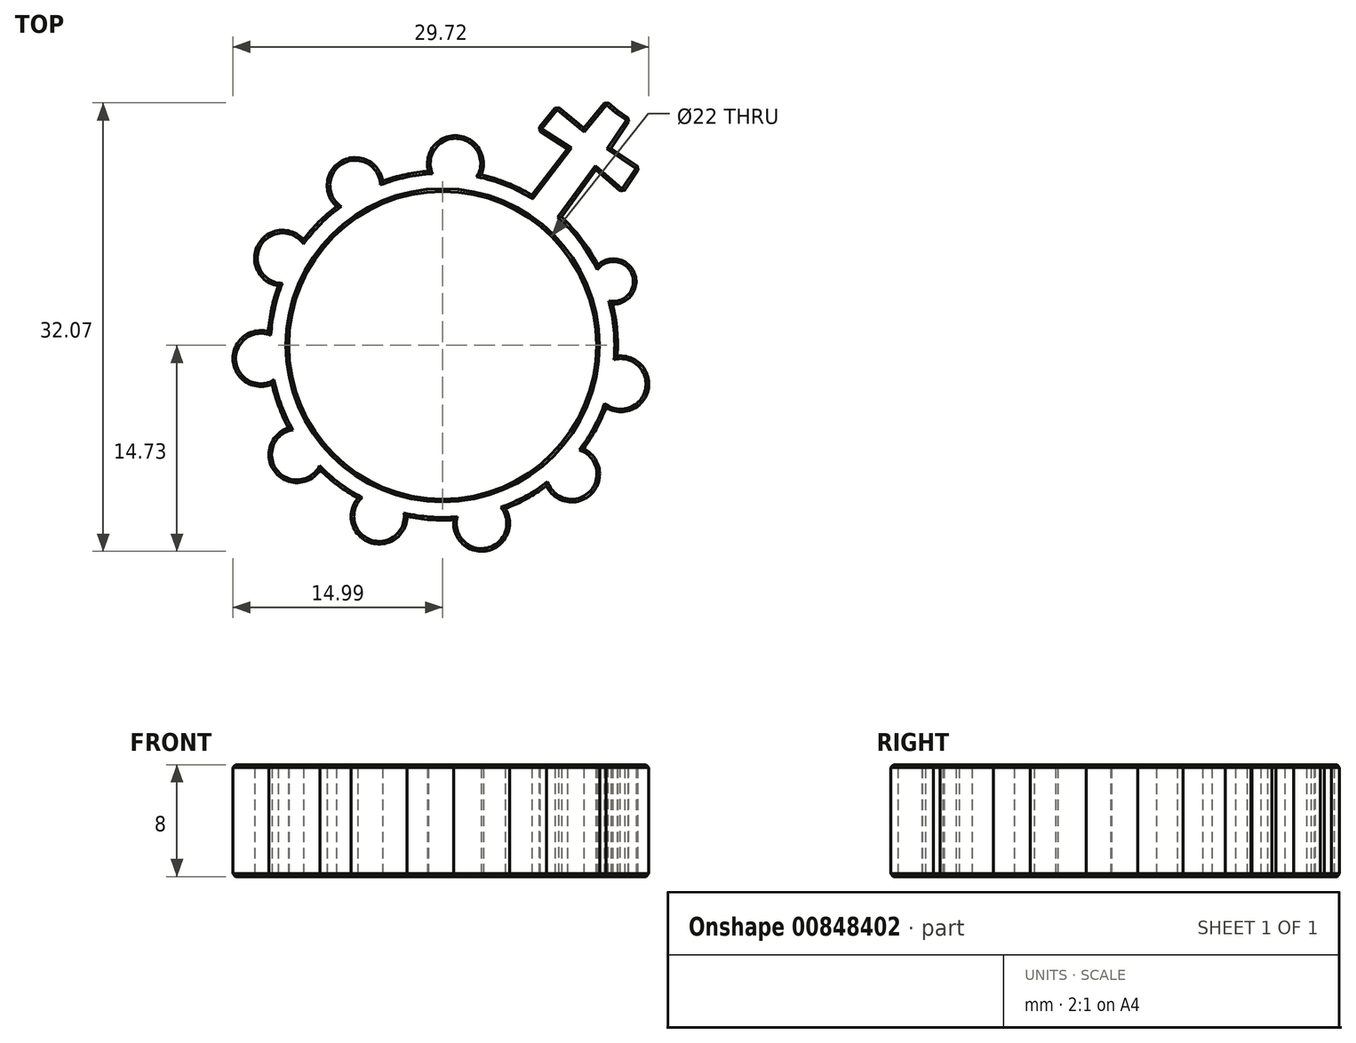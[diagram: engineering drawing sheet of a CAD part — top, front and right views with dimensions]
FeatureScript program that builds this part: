
annotation { "Feature Type Name" : "Feature", "Feature Type Description" : "" }
export const myFeature = defineFeature(function(context is Context, id is Id, definition is map)
    precondition{}
    {
        {
            var Q0;
            Q0=qCreatedBy(makeId("Top.planeOp"),FACE);
            var sketch = newSketch(context, id + "F0", { "sketchPlane" : qUnion([Q0])});
            skCircle(sketch, "E0", {"center": v(0, 0) * mm, "radius": 11 * mm});
            skCircle(sketch, "E1", {"center": v(0, 0) * mm, "radius": 12.5 * mm});
            skCircle(sketch, "E2.cCircle", {"center": v(0, 0) * mm, "radius": 12.5 * mm, "construction": true});
            skLineSegment(sketch, "E2.0", {"start": v(9.22, -9.2) * mm, "end": v(2.78, -12.73) * mm});
            skLineSegment(sketch, "E2.1", {"start": v(2.78, -12.73) * mm, "end": v(-4.54, -12.21) * mm});
            skLineSegment(sketch, "E2.2", {"start": v(-4.54, -12.21) * mm, "end": v(-10.42, -7.82) * mm});
            skLineSegment(sketch, "E2.3", {"start": v(-10.42, -7.82) * mm, "end": v(-13, -0.94) * mm});
            skLineSegment(sketch, "E2.4", {"start": v(-13, -0.94) * mm, "end": v(-11.44, 6.23) * mm});
            skLineSegment(sketch, "E2.5", {"start": v(-11.44, 6.23) * mm, "end": v(-6.25, 11.43) * mm});
            skLineSegment(sketch, "E2.6", {"start": v(-6.25, 11.43) * mm, "end": v(0.92, 13) * mm});
            skLineSegment(sketch, "E2.7", {"start": v(0.92, 13) * mm, "end": v(7.8, 10.44) * mm});
            skLineSegment(sketch, "E2.8", {"start": v(7.8, 10.44) * mm, "end": v(12.2, 4.56) * mm});
            skLineSegment(sketch, "E2.9", {"start": v(12.2, 4.56) * mm, "end": v(12.73, -2.76) * mm});
            skLineSegment(sketch, "E2.10", {"start": v(12.73, -2.76) * mm, "end": v(9.22, -9.2) * mm});
            skPoint(sketch, "E2.0.midPoint", {"position": v(6, -10.97) * mm});
            skCircle(sketch, "E3", {"center": v(0.92, 13) * mm, "radius": 2 * mm});
            skCircle(sketch, "E4", {"center": v(-6.25, 11.43) * mm, "radius": 2 * mm});
            skCircle(sketch, "E5", {"center": v(-11.44, 6.23) * mm, "radius": 2 * mm});
            skCircle(sketch, "E6", {"center": v(-13, -0.94) * mm, "radius": 2 * mm});
            skCircle(sketch, "E7", {"center": v(-10.42, -7.82) * mm, "radius": 2 * mm});
            skCircle(sketch, "E8", {"center": v(-4.54, -12.21) * mm, "radius": 2 * mm});
            skCircle(sketch, "E9", {"center": v(2.78, -12.73) * mm, "radius": 2 * mm});
            skCircle(sketch, "E10", {"center": v(9.22, -9.2) * mm, "radius": 2 * mm});
            skCircle(sketch, "E11", {"center": v(12.73, -2.76) * mm, "radius": 2 * mm});
            skCircle(sketch, "E12", {"center": v(12.2, 4.56) * mm, "radius": 1.62 * mm});
            skLineSegment(sketch, "E13", {"start": v(0, 0) * mm, "end": v(12.63, 16.93) * mm, "construction": true});
            skLineSegment(sketch, "E14", {"start": v(6.38, 10.75) * mm, "end": v(8.92, 14.06) * mm});
            skLineSegment(sketch, "E15", {"start": v(8.92, 14.06) * mm, "end": v(6.77, 15.44) * mm});
            skLineSegment(sketch, "E16", {"start": v(6.77, 15.44) * mm, "end": v(8.16, 17.12) * mm});
            skLineSegment(sketch, "E17", {"start": v(8.16, 17.12) * mm, "end": v(10.08, 15.53) * mm});
            skLineSegment(sketch, "E18", {"start": v(10.08, 15.53) * mm, "end": v(11.67, 17.46) * mm});
            skLineSegment(sketch, "E19", {"start": v(11.67, 17.46) * mm, "end": v(12.51, 16.77) * mm});
            skLineSegment(sketch, "E20.MirrorCS", {"start": v(13.41, 16.16) * mm, "end": v(12.51, 16.77) * mm});
            skLineSegment(sketch, "E21.MirrorCS", {"start": v(12.02, 14.1) * mm, "end": v(13.41, 16.16) * mm});
            skLineSegment(sketch, "E22.MirrorCS", {"start": v(14.09, 12.7) * mm, "end": v(12.02, 14.1) * mm});
            skLineSegment(sketch, "E23.MirrorCS", {"start": v(12.87, 10.9) * mm, "end": v(14.09, 12.7) * mm});
            skLineSegment(sketch, "E24.MirrorCS", {"start": v(10.94, 12.56) * mm, "end": v(12.87, 10.9) * mm});
            skLineSegment(sketch, "E25.MirrorCS", {"start": v(8.49, 9.18) * mm, "end": v(10.94, 12.56) * mm});
            skSolve(sketch);
        }
        {
            var Q0;
            Q0=makeQuery(id+"F0.imprint","IMPRINT",FACE,{"disambiguationData":[TD([[makeQuery(id+"F0.imprint","IMPRINT",EDGE,{"derivedFrom":sQuery(id+"F0.wireOp",EDGE,"E0")}),-1.0]])]});
            var Q1;
            {var subQ0=sQuery(id+"F0.wireOp",EDGE,"E2.7");var subQ1=sQuery(id+"F0.wireOp",EDGE,"E2.6");var subQ2=makeQuery(id+"F0.imprint","INTERSECT",VERTEX,{"derivedFrom":[subQ1,subQ0]});Q1=makeQuery(id+"F0.imprint","IMPRINT",FACE,{"disambiguationData":[TD([[makeQuery(id+"F0.imprint","IMPRINT",EDGE,{"disambiguationData":[TD([[subQ2,1.0]])],"derivedFrom":subQ1}),1.0]])]});}
            var Q2;
            {var subQ5=sQuery(id+"F0.wireOp",EDGE,"E15");Q2=makeQuery(id+"F0.imprint","IMPRINT",FACE,{"disambiguationData":[TD([[makeQuery(id+"F0.imprint","IMPRINT",EDGE,{"derivedFrom":subQ5}),-1.0]])]});}
            var Q3;
            {var subQ0=sQuery(id+"F0.wireOp",EDGE,"E14");var subQ1=sQuery(id+"F0.wireOp",EDGE,"E1");var subQ2=makeQuery(id+"F0.imprint","INTERSECT",VERTEX,{"derivedFrom":[subQ1,subQ0]});Q3=makeQuery(id+"F0.imprint","IMPRINT",FACE,{"disambiguationData":[TD([[makeQuery(id+"F0.imprint","IMPRINT",EDGE,{"disambiguationData":[TD([[subQ2,1.0]])],"derivedFrom":subQ1}),-1.0]])]});}
            var Q4;
            {var subQ0=sQuery(id+"F0.wireOp",EDGE,"E2.9");var subQ1=sQuery(id+"F0.wireOp",EDGE,"E2.8");var subQ2=makeQuery(id+"F0.imprint","INTERSECT",VERTEX,{"derivedFrom":[subQ1,subQ0]});Q4=makeQuery(id+"F0.imprint","IMPRINT",FACE,{"disambiguationData":[TD([[makeQuery(id+"F0.imprint","IMPRINT",EDGE,{"disambiguationData":[TD([[subQ2,1.0]])],"derivedFrom":subQ1}),1.0]])]});}
            var Q5;
            {var subQ0=sQuery(id+"F0.wireOp",EDGE,"E12");var subQ1=sQuery(id+"F0.wireOp",EDGE,"E1");var subQ2=makeQuery(id+"F0.imprint","INTERSECT",VERTEX,{"disambiguationData":[OD(0.0)],"derivedFrom":[subQ1,subQ0]});Q5=makeQuery(id+"F0.imprint","IMPRINT",FACE,{"disambiguationData":[TD([[makeQuery(id+"F0.imprint","IMPRINT",EDGE,{"disambiguationData":[TD([[subQ2,-1.0]])],"derivedFrom":subQ1}),1.0]])]});}
            var Q6;
            {var subQ0=sQuery(id+"F0.wireOp",EDGE,"E2.10");var subQ1=sQuery(id+"F0.wireOp",EDGE,"E2.9");var subQ2=makeQuery(id+"F0.imprint","INTERSECT",VERTEX,{"derivedFrom":[subQ1,subQ0]});Q6=makeQuery(id+"F0.imprint","IMPRINT",FACE,{"disambiguationData":[TD([[makeQuery(id+"F0.imprint","IMPRINT",EDGE,{"disambiguationData":[TD([[subQ2,1.0]])],"derivedFrom":subQ1}),1.0]])]});}
            var Q7;
            {var subQ0=sQuery(id+"F0.wireOp",EDGE,"E2.10");var subQ1=sQuery(id+"F0.wireOp",EDGE,"E2.0");var subQ2=makeQuery(id+"F0.imprint","INTERSECT",VERTEX,{"derivedFrom":[subQ1,subQ0]});Q7=makeQuery(id+"F0.imprint","IMPRINT",FACE,{"disambiguationData":[TD([[makeQuery(id+"F0.imprint","IMPRINT",EDGE,{"disambiguationData":[TD([[subQ2,-1.0]])],"derivedFrom":subQ1}),1.0]])]});}
            var Q8;
            {var subQ0=sQuery(id+"F0.wireOp",EDGE,"E2.1");var subQ1=sQuery(id+"F0.wireOp",EDGE,"E2.0");var subQ2=makeQuery(id+"F0.imprint","INTERSECT",VERTEX,{"derivedFrom":[subQ1,subQ0]});Q8=makeQuery(id+"F0.imprint","IMPRINT",FACE,{"disambiguationData":[TD([[makeQuery(id+"F0.imprint","IMPRINT",EDGE,{"disambiguationData":[TD([[subQ2,1.0]])],"derivedFrom":subQ1}),1.0]])]});}
            var Q9;
            {var subQ0=sQuery(id+"F0.wireOp",EDGE,"E2.2");var subQ1=sQuery(id+"F0.wireOp",EDGE,"E2.1");var subQ2=makeQuery(id+"F0.imprint","INTERSECT",VERTEX,{"derivedFrom":[subQ1,subQ0]});Q9=makeQuery(id+"F0.imprint","IMPRINT",FACE,{"disambiguationData":[TD([[makeQuery(id+"F0.imprint","IMPRINT",EDGE,{"disambiguationData":[TD([[subQ2,1.0]])],"derivedFrom":subQ1}),1.0]])]});}
            var Q10;
            {var subQ0=sQuery(id+"F0.wireOp",EDGE,"E2.3");var subQ1=sQuery(id+"F0.wireOp",EDGE,"E2.2");var subQ2=makeQuery(id+"F0.imprint","INTERSECT",VERTEX,{"derivedFrom":[subQ1,subQ0]});Q10=makeQuery(id+"F0.imprint","IMPRINT",FACE,{"disambiguationData":[TD([[makeQuery(id+"F0.imprint","IMPRINT",EDGE,{"disambiguationData":[TD([[subQ2,1.0]])],"derivedFrom":subQ1}),1.0]])]});}
            var Q11;
            {var subQ0=sQuery(id+"F0.wireOp",EDGE,"E2.4");var subQ1=sQuery(id+"F0.wireOp",EDGE,"E2.3");var subQ2=makeQuery(id+"F0.imprint","INTERSECT",VERTEX,{"derivedFrom":[subQ1,subQ0]});Q11=makeQuery(id+"F0.imprint","IMPRINT",FACE,{"disambiguationData":[TD([[makeQuery(id+"F0.imprint","IMPRINT",EDGE,{"disambiguationData":[TD([[subQ2,1.0]])],"derivedFrom":subQ1}),1.0]])]});}
            var Q12;
            {var subQ0=sQuery(id+"F0.wireOp",EDGE,"E2.5");var subQ1=sQuery(id+"F0.wireOp",EDGE,"E2.4");var subQ2=makeQuery(id+"F0.imprint","INTERSECT",VERTEX,{"derivedFrom":[subQ1,subQ0]});Q12=makeQuery(id+"F0.imprint","IMPRINT",FACE,{"disambiguationData":[TD([[makeQuery(id+"F0.imprint","IMPRINT",EDGE,{"disambiguationData":[TD([[subQ2,1.0]])],"derivedFrom":subQ1}),1.0]])]});}
            var Q13;
            {var subQ0=sQuery(id+"F0.wireOp",EDGE,"E2.6");var subQ1=sQuery(id+"F0.wireOp",EDGE,"E2.5");var subQ2=makeQuery(id+"F0.imprint","INTERSECT",VERTEX,{"derivedFrom":[subQ1,subQ0]});Q13=makeQuery(id+"F0.imprint","IMPRINT",FACE,{"disambiguationData":[TD([[makeQuery(id+"F0.imprint","IMPRINT",EDGE,{"disambiguationData":[TD([[subQ2,1.0]])],"derivedFrom":subQ1}),1.0]])]});}
            var Q14;
            {var subQ0=sQuery(id+"F0.wireOp",EDGE,"E4");var subQ1=sQuery(id+"F0.wireOp",EDGE,"E1");var subQ2=makeQuery(id+"F0.imprint","INTERSECT",VERTEX,{"disambiguationData":[OD(0.0)],"derivedFrom":[subQ1,subQ0]});Q14=makeQuery(id+"F0.imprint","IMPRINT",FACE,{"disambiguationData":[TD([[makeQuery(id+"F0.imprint","IMPRINT",EDGE,{"disambiguationData":[TD([[subQ2,-1.0]])],"derivedFrom":subQ1}),1.0]])]});}
            var Q15;
            {var subQ0=sQuery(id+"F0.wireOp",EDGE,"E5");var subQ1=sQuery(id+"F0.wireOp",EDGE,"E1");var subQ2=makeQuery(id+"F0.imprint","INTERSECT",VERTEX,{"disambiguationData":[OD(0.0)],"derivedFrom":[subQ1,subQ0]});Q15=makeQuery(id+"F0.imprint","IMPRINT",FACE,{"disambiguationData":[TD([[makeQuery(id+"F0.imprint","IMPRINT",EDGE,{"disambiguationData":[TD([[subQ2,-1.0]])],"derivedFrom":subQ1}),1.0]])]});}
            var Q16;
            {var subQ0=sQuery(id+"F0.wireOp",EDGE,"E6");var subQ1=sQuery(id+"F0.wireOp",EDGE,"E1");var subQ2=makeQuery(id+"F0.imprint","INTERSECT",VERTEX,{"disambiguationData":[OD(0.0)],"derivedFrom":[subQ1,subQ0]});Q16=makeQuery(id+"F0.imprint","IMPRINT",FACE,{"disambiguationData":[TD([[makeQuery(id+"F0.imprint","IMPRINT",EDGE,{"disambiguationData":[TD([[subQ2,-1.0]])],"derivedFrom":subQ1}),1.0]])]});}
            var Q17;
            {var subQ0=sQuery(id+"F0.wireOp",EDGE,"E7");var subQ1=sQuery(id+"F0.wireOp",EDGE,"E1");var subQ2=makeQuery(id+"F0.imprint","INTERSECT",VERTEX,{"disambiguationData":[OD(0.0)],"derivedFrom":[subQ1,subQ0]});Q17=makeQuery(id+"F0.imprint","IMPRINT",FACE,{"disambiguationData":[TD([[makeQuery(id+"F0.imprint","IMPRINT",EDGE,{"disambiguationData":[TD([[subQ2,-1.0]])],"derivedFrom":subQ1}),1.0]])]});}
            var Q18;
            {var subQ0=sQuery(id+"F0.wireOp",EDGE,"E11");var subQ1=sQuery(id+"F0.wireOp",EDGE,"E1");var subQ2=makeQuery(id+"F0.imprint","INTERSECT",VERTEX,{"disambiguationData":[OD(0.0)],"derivedFrom":[subQ1,subQ0]});Q18=makeQuery(id+"F0.imprint","IMPRINT",FACE,{"disambiguationData":[TD([[makeQuery(id+"F0.imprint","IMPRINT",EDGE,{"disambiguationData":[TD([[subQ2,-1.0]])],"derivedFrom":subQ1}),1.0]])]});}
            var Q19;
            {var subQ0=sQuery(id+"F0.wireOp",EDGE,"E8");var subQ1=sQuery(id+"F0.wireOp",EDGE,"E1");var subQ2=makeQuery(id+"F0.imprint","INTERSECT",VERTEX,{"disambiguationData":[OD(0.0)],"derivedFrom":[subQ1,subQ0]});Q19=makeQuery(id+"F0.imprint","IMPRINT",FACE,{"disambiguationData":[TD([[makeQuery(id+"F0.imprint","IMPRINT",EDGE,{"disambiguationData":[TD([[subQ2,-1.0]])],"derivedFrom":subQ1}),1.0]])]});}
            var Q20;
            {var subQ0=sQuery(id+"F0.wireOp",EDGE,"E10");var subQ1=sQuery(id+"F0.wireOp",EDGE,"E1");var subQ2=makeQuery(id+"F0.imprint","INTERSECT",VERTEX,{"disambiguationData":[OD(0.0)],"derivedFrom":[subQ1,subQ0]});Q20=makeQuery(id+"F0.imprint","IMPRINT",FACE,{"disambiguationData":[TD([[makeQuery(id+"F0.imprint","IMPRINT",EDGE,{"disambiguationData":[TD([[subQ2,-1.0]])],"derivedFrom":subQ1}),1.0]])]});}
            var Q21;
            {var subQ0=sQuery(id+"F0.wireOp",EDGE,"E3");var subQ1=sQuery(id+"F0.wireOp",EDGE,"E1");var subQ2=makeQuery(id+"F0.imprint","INTERSECT",VERTEX,{"disambiguationData":[OD(0.0)],"derivedFrom":[subQ1,subQ0]});Q21=makeQuery(id+"F0.imprint","IMPRINT",FACE,{"disambiguationData":[TD([[makeQuery(id+"F0.imprint","IMPRINT",EDGE,{"disambiguationData":[TD([[subQ2,-1.0]])],"derivedFrom":subQ1}),1.0]])]});}
            var Q22;
            {var subQ0=sQuery(id+"F0.wireOp",EDGE,"E9");var subQ1=sQuery(id+"F0.wireOp",EDGE,"E1");var subQ2=makeQuery(id+"F0.imprint","INTERSECT",VERTEX,{"disambiguationData":[OD(0.0)],"derivedFrom":[subQ1,subQ0]});Q22=makeQuery(id+"F0.imprint","IMPRINT",FACE,{"disambiguationData":[TD([[makeQuery(id+"F0.imprint","IMPRINT",EDGE,{"disambiguationData":[TD([[subQ2,-1.0]])],"derivedFrom":subQ1}),1.0]])]});}
            var Q23;
            {var subQ3=sQuery(id+"F0.wireOp",EDGE,"E3");var subQ6=sQuery(id+"F0.wireOp",EDGE,"E1");var subQ8=makeQuery(id+"F0.imprint","INTERSECT",VERTEX,{"disambiguationData":[OD(0.0)],"derivedFrom":[subQ6,subQ3]});Q23=makeQuery(id+"F0.imprint","IMPRINT",FACE,{"disambiguationData":[TD([[makeQuery(id+"F0.imprint","IMPRINT",EDGE,{"disambiguationData":[TD([[subQ8,-1.0]])],"derivedFrom":subQ6}),-1.0]])]});}
            var Q24;
            {var subQ3=sQuery(id+"F0.wireOp",EDGE,"E4");var subQ5=sQuery(id+"F0.wireOp",EDGE,"E1");var subQ6=makeQuery(id+"F0.imprint","INTERSECT",VERTEX,{"disambiguationData":[OD(0.0)],"derivedFrom":[subQ5,subQ3]});Q24=makeQuery(id+"F0.imprint","IMPRINT",FACE,{"disambiguationData":[TD([[makeQuery(id+"F0.imprint","IMPRINT",EDGE,{"disambiguationData":[TD([[subQ6,-1.0]])],"derivedFrom":subQ5}),-1.0]])]});}
            var Q25;
            {var subQ0=sQuery(id+"F0.wireOp",EDGE,"E5");var subQ3=sQuery(id+"F0.wireOp",EDGE,"E1");var subQ4=makeQuery(id+"F0.imprint","INTERSECT",VERTEX,{"disambiguationData":[OD(0.0)],"derivedFrom":[subQ3,subQ0]});Q25=makeQuery(id+"F0.imprint","IMPRINT",FACE,{"disambiguationData":[TD([[makeQuery(id+"F0.imprint","IMPRINT",EDGE,{"disambiguationData":[TD([[subQ4,-1.0]])],"derivedFrom":subQ3}),-1.0]])]});}
            var Q26;
            {var subQ0=sQuery(id+"F0.wireOp",EDGE,"E6");var subQ3=sQuery(id+"F0.wireOp",EDGE,"E1");var subQ4=makeQuery(id+"F0.imprint","INTERSECT",VERTEX,{"disambiguationData":[OD(0.0)],"derivedFrom":[subQ3,subQ0]});Q26=makeQuery(id+"F0.imprint","IMPRINT",FACE,{"disambiguationData":[TD([[makeQuery(id+"F0.imprint","IMPRINT",EDGE,{"disambiguationData":[TD([[subQ4,-1.0]])],"derivedFrom":subQ3}),-1.0]])]});}
            var Q27;
            {var subQ0=sQuery(id+"F0.wireOp",EDGE,"E7");var subQ3=sQuery(id+"F0.wireOp",EDGE,"E1");var subQ4=makeQuery(id+"F0.imprint","INTERSECT",VERTEX,{"disambiguationData":[OD(0.0)],"derivedFrom":[subQ3,subQ0]});Q27=makeQuery(id+"F0.imprint","IMPRINT",FACE,{"disambiguationData":[TD([[makeQuery(id+"F0.imprint","IMPRINT",EDGE,{"disambiguationData":[TD([[subQ4,-1.0]])],"derivedFrom":subQ3}),-1.0]])]});}
            var Q28;
            {var subQ3=sQuery(id+"F0.wireOp",EDGE,"E8");var subQ6=sQuery(id+"F0.wireOp",EDGE,"E1");var subQ7=makeQuery(id+"F0.imprint","INTERSECT",VERTEX,{"disambiguationData":[OD(0.0)],"derivedFrom":[subQ6,subQ3]});Q28=makeQuery(id+"F0.imprint","IMPRINT",FACE,{"disambiguationData":[TD([[makeQuery(id+"F0.imprint","IMPRINT",EDGE,{"disambiguationData":[TD([[subQ7,-1.0]])],"derivedFrom":subQ6}),-1.0]])]});}
            var Q29;
            {var subQ3=sQuery(id+"F0.wireOp",EDGE,"E9");var subQ5=sQuery(id+"F0.wireOp",EDGE,"E1");var subQ6=makeQuery(id+"F0.imprint","INTERSECT",VERTEX,{"disambiguationData":[OD(0.0)],"derivedFrom":[subQ5,subQ3]});Q29=makeQuery(id+"F0.imprint","IMPRINT",FACE,{"disambiguationData":[TD([[makeQuery(id+"F0.imprint","IMPRINT",EDGE,{"disambiguationData":[TD([[subQ6,-1.0]])],"derivedFrom":subQ5}),-1.0]])]});}
            var Q30;
            {var subQ0=sQuery(id+"F0.wireOp",EDGE,"E10");var subQ3=sQuery(id+"F0.wireOp",EDGE,"E1");var subQ5=makeQuery(id+"F0.imprint","INTERSECT",VERTEX,{"disambiguationData":[OD(0.0)],"derivedFrom":[subQ3,subQ0]});Q30=makeQuery(id+"F0.imprint","IMPRINT",FACE,{"disambiguationData":[TD([[makeQuery(id+"F0.imprint","IMPRINT",EDGE,{"disambiguationData":[TD([[subQ5,-1.0]])],"derivedFrom":subQ3}),-1.0]])]});}
            var Q31;
            {var subQ0=sQuery(id+"F0.wireOp",EDGE,"E11");var subQ3=sQuery(id+"F0.wireOp",EDGE,"E1");var subQ8=makeQuery(id+"F0.imprint","INTERSECT",VERTEX,{"disambiguationData":[OD(0.0)],"derivedFrom":[subQ3,subQ0]});Q31=makeQuery(id+"F0.imprint","IMPRINT",FACE,{"disambiguationData":[TD([[makeQuery(id+"F0.imprint","IMPRINT",EDGE,{"disambiguationData":[TD([[subQ8,-1.0]])],"derivedFrom":subQ3}),-1.0]])]});}
            var Q32;
            {var subQ3=sQuery(id+"F0.wireOp",EDGE,"E12");var subQ6=sQuery(id+"F0.wireOp",EDGE,"E1");var subQ8=makeQuery(id+"F0.imprint","INTERSECT",VERTEX,{"disambiguationData":[OD(0.0)],"derivedFrom":[subQ6,subQ3]});Q32=makeQuery(id+"F0.imprint","IMPRINT",FACE,{"disambiguationData":[TD([[makeQuery(id+"F0.imprint","IMPRINT",EDGE,{"disambiguationData":[TD([[subQ8,-1.0]])],"derivedFrom":subQ6}),-1.0]])]});}
            extrude(context, id + "F1", {"entities" : qUnion([Q0, Q1, Q2, Q3, Q4, Q5, Q6, Q7, Q8, Q9, Q10, Q11, Q12, Q13, Q14, Q15, Q16, Q17, Q18, Q19, Q20, Q21, Q22, Q23, Q24, Q25, Q26, Q27, Q28, Q29, Q30, Q31, Q32]), "endBound" : BoundingType.SYMMETRIC, "depth" : 8 * mm, "offsetDistance" : 25 * mm});
        }
        {
            var Q0;
            Q0=makeQuery(id+"F1.opExtrude","CAP_FACE",FACE,{"disambiguationData":[OSD([sQuery(id+"F0.wireOp",EDGE,"E0"),sQuery(id+"F0.wireOp",EDGE,"E1"),sQuery(id+"F0.wireOp",EDGE,"E3"),sQuery(id+"F0.wireOp",EDGE,"E4"),sQuery(id+"F0.wireOp",EDGE,"E5"),sQuery(id+"F0.wireOp",EDGE,"E6"),sQuery(id+"F0.wireOp",EDGE,"E7"),sQuery(id+"F0.wireOp",EDGE,"E8"),sQuery(id+"F0.wireOp",EDGE,"E9"),sQuery(id+"F0.wireOp",EDGE,"E10"),sQuery(id+"F0.wireOp",EDGE,"E11"),sQuery(id+"F0.wireOp",EDGE,"E12"),sQuery(id+"F0.wireOp",EDGE,"E14"),sQuery(id+"F0.wireOp",EDGE,"E15"),sQuery(id+"F0.wireOp",EDGE,"E16"),sQuery(id+"F0.wireOp",EDGE,"E17"),sQuery(id+"F0.wireOp",EDGE,"E18"),sQuery(id+"F0.wireOp",EDGE,"E19"),sQuery(id+"F0.wireOp",EDGE,"E20.MirrorCS"),sQuery(id+"F0.wireOp",EDGE,"E21.MirrorCS"),sQuery(id+"F0.wireOp",EDGE,"E22.MirrorCS"),sQuery(id+"F0.wireOp",EDGE,"E23.MirrorCS"),sQuery(id+"F0.wireOp",EDGE,"E24.MirrorCS"),sQuery(id+"F0.wireOp",EDGE,"E25.MirrorCS")])],"isStart":true});
            var Q1;
            Q1=makeQuery(id+"F1.opExtrude","CAP_FACE",FACE,{"disambiguationData":[OSD([sQuery(id+"F0.wireOp",EDGE,"E0"),sQuery(id+"F0.wireOp",EDGE,"E1"),sQuery(id+"F0.wireOp",EDGE,"E3"),sQuery(id+"F0.wireOp",EDGE,"E4"),sQuery(id+"F0.wireOp",EDGE,"E5"),sQuery(id+"F0.wireOp",EDGE,"E6"),sQuery(id+"F0.wireOp",EDGE,"E7"),sQuery(id+"F0.wireOp",EDGE,"E8"),sQuery(id+"F0.wireOp",EDGE,"E9"),sQuery(id+"F0.wireOp",EDGE,"E10"),sQuery(id+"F0.wireOp",EDGE,"E11"),sQuery(id+"F0.wireOp",EDGE,"E12"),sQuery(id+"F0.wireOp",EDGE,"E14"),sQuery(id+"F0.wireOp",EDGE,"E15"),sQuery(id+"F0.wireOp",EDGE,"E16"),sQuery(id+"F0.wireOp",EDGE,"E17"),sQuery(id+"F0.wireOp",EDGE,"E18"),sQuery(id+"F0.wireOp",EDGE,"E19"),sQuery(id+"F0.wireOp",EDGE,"E20.MirrorCS"),sQuery(id+"F0.wireOp",EDGE,"E21.MirrorCS"),sQuery(id+"F0.wireOp",EDGE,"E22.MirrorCS"),sQuery(id+"F0.wireOp",EDGE,"E23.MirrorCS"),sQuery(id+"F0.wireOp",EDGE,"E24.MirrorCS"),sQuery(id+"F0.wireOp",EDGE,"E25.MirrorCS")])],"isStart":false});
            var Q2;
            Q2=makeQuery(id+"F1.opExtrude","SWEPT_EDGE",EDGE,{"disambiguationData":[OSD([sQuery(id+"F0.wireOp",EDGE,"E23.MirrorCS"),sQuery(id+"F0.wireOp",EDGE,"E24.MirrorCS")])]});
            var Q3;
            Q3=makeQuery(id+"F1.opExtrude","SWEPT_EDGE",EDGE,{"disambiguationData":[OSD([sQuery(id+"F0.wireOp",EDGE,"E22.MirrorCS"),sQuery(id+"F0.wireOp",EDGE,"E23.MirrorCS")])]});
            var Q4;
            Q4=makeQuery(id+"F1.opExtrude","SWEPT_EDGE",EDGE,{"disambiguationData":[OSD([sQuery(id+"F0.wireOp",EDGE,"E20.MirrorCS"),sQuery(id+"F0.wireOp",EDGE,"E21.MirrorCS")])]});
            var Q5;
            Q5=makeQuery(id+"F1.opExtrude","SWEPT_EDGE",EDGE,{"disambiguationData":[OSD([sQuery(id+"F0.wireOp",EDGE,"E18"),sQuery(id+"F0.wireOp",EDGE,"E19")])]});
            var Q6;
            Q6=makeQuery(id+"F1.opExtrude","SWEPT_EDGE",EDGE,{"disambiguationData":[OSD([sQuery(id+"F0.wireOp",EDGE,"E16"),sQuery(id+"F0.wireOp",EDGE,"E17")])]});
            var Q7;
            Q7=makeQuery(id+"F1.opExtrude","SWEPT_EDGE",EDGE,{"disambiguationData":[OSD([sQuery(id+"F0.wireOp",EDGE,"E15"),sQuery(id+"F0.wireOp",EDGE,"E16")])]});
            chamfer(context, id + "F2", {"entities" : qUnion([Q0, Q1, Q2, Q3, Q4, Q5, Q6, Q7]), "width" : .2 * mm, "tangentPropagation" : true});
        }
    });
